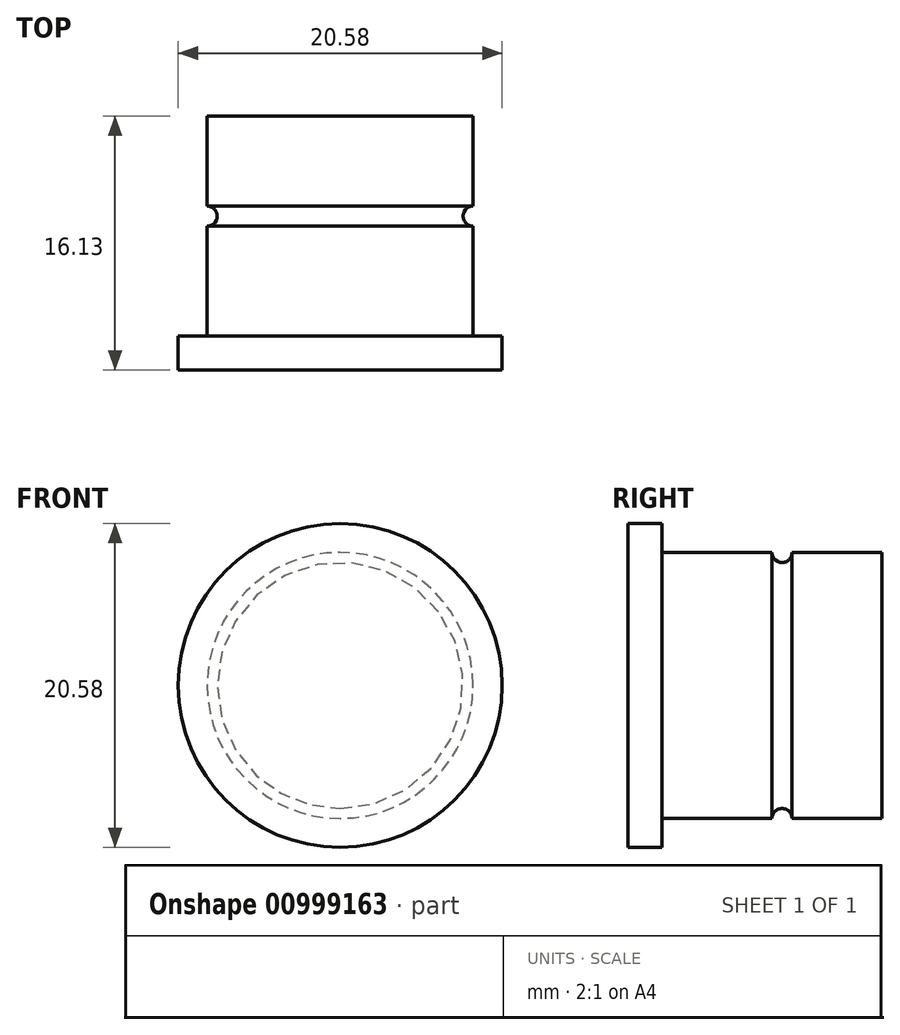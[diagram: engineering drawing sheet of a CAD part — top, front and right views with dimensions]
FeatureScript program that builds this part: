
annotation { "Feature Type Name" : "Feature", "Feature Type Description" : "" }
export const myFeature = defineFeature(function(context is Context, id is Id, definition is map)
    precondition{}
    {
        {
            var Q0;
            Q0=qCreatedBy(makeId("Right.planeOp"),FACE);
            var sketch = newSketch(context, id + "F0", { "sketchPlane" : qUnion([Q0])});
            skLineSegment(sketch, "E0", {"start": v(-9.53, 0) * mm, "end": v(-7.37, 0) * mm});
            skLineSegment(sketch, "E1", {"start": v(-7.37, 0) * mm, "end": v(6.6, 0) * mm});
            skLineSegment(sketch, "E2", {"start": v(6.6, 0) * mm, "end": v(6.6, 8.45) * mm});
            skLineSegment(sketch, "E3", {"start": v(6.6, 8.45) * mm, "end": v(3.66, 8.45) * mm});
            skLineSegment(sketch, "E4", {"start": v(3.66, 8.45) * mm, "end": v(0.88, 8.45) * mm});
            skLineSegment(sketch, "E5", {"start": v(-3.17, 8.45) * mm, "end": v(-7.37, 8.45) * mm});
            skLineSegment(sketch, "E6", {"start": v(-7.37, 8.45) * mm, "end": v(-7.37, 10.29) * mm});
            skLineSegment(sketch, "E7", {"start": v(-7.37, 10.29) * mm, "end": v(-9.53, 10.29) * mm});
            skLineSegment(sketch, "E8", {"start": v(-9.53, 10.29) * mm, "end": v(-9.53, 0) * mm});
            skArc(sketch, "E9", {"start": v(-0.39, 8.45) * mm, "mid": v(0.25, 7.81) * mm, "end": v(0.88, 8.45) * mm});
            skLineSegment(sketch, "E10.trimOffspring", {"start": v(-0.39, 8.45) * mm, "end": v(-3.17, 8.45) * mm});
            skSolve(sketch);
        }
        {
            var Q0;
            Q0 = qSketchRegion(id + "F0", true);
            var Q1;
            Q1=sQuery(id+"F0.wireOp",EDGE,"E1");
            revolve(context, id + "F1", {"surfaceOperationType" : NewSurfaceOperationType.NEW, "entities" : qUnion([Q0]), "axis" : qUnion([Q1]), "revolveType" : RevolveType.FULL});
        }
    });
